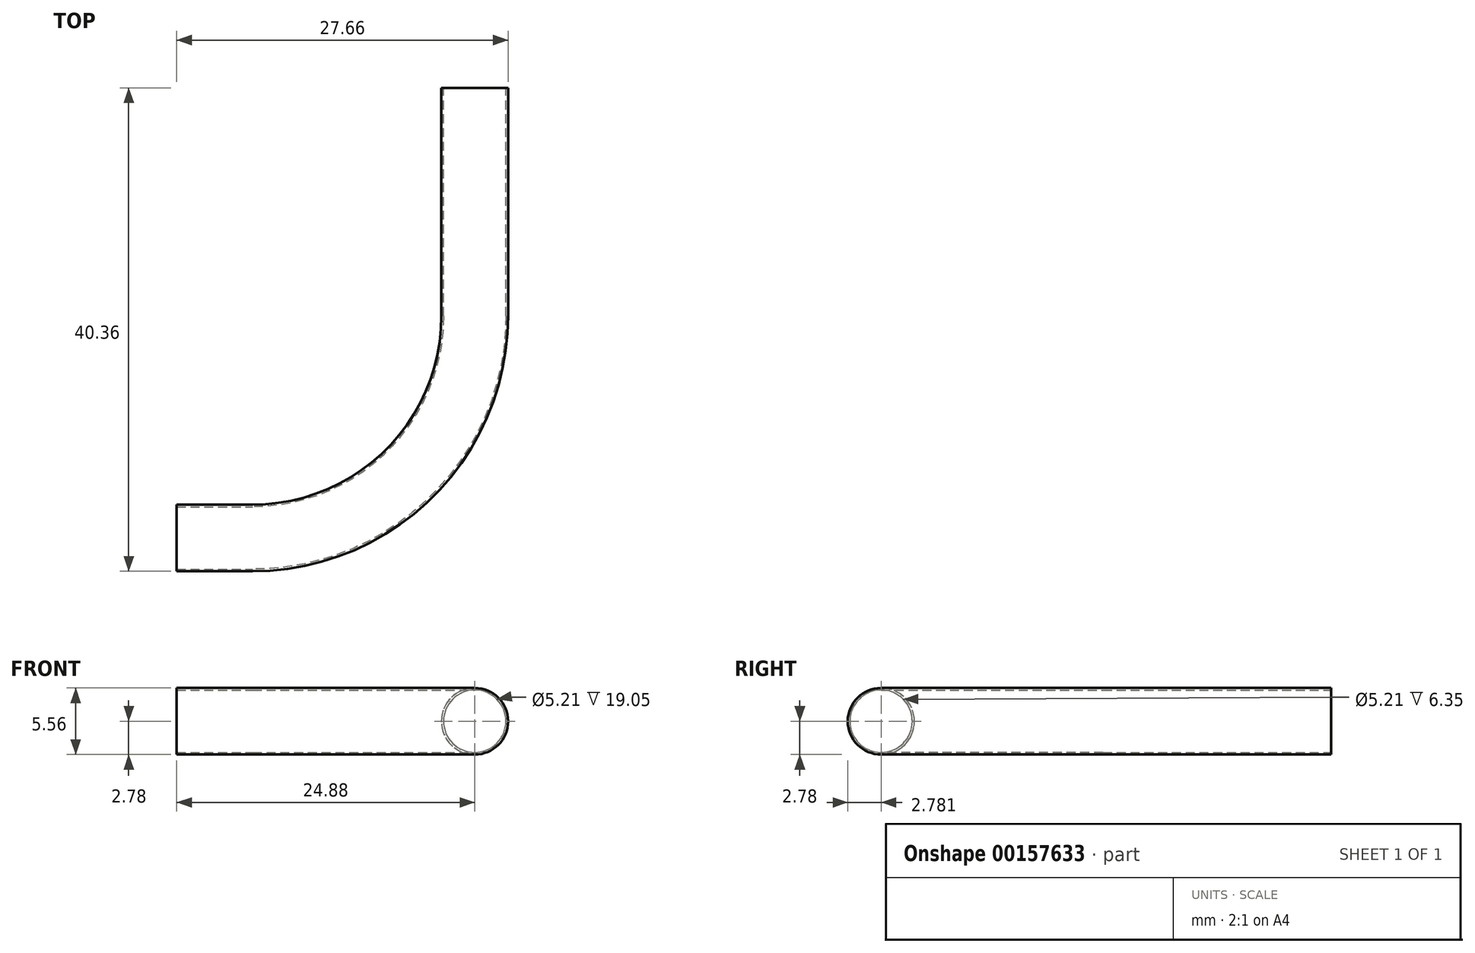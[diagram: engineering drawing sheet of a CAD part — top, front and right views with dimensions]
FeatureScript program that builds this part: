
annotation { "Feature Type Name" : "Feature", "Feature Type Description" : "" }
export const myFeature = defineFeature(function(context is Context, id is Id, definition is map)
    precondition{}
    {
        {
            var Q0;
            Q0=qCreatedBy(makeId("Front.planeOp"),FACE);
            var sketch = newSketch(context, id + "F0", { "sketchPlane" : qUnion([Q0])});
            skCircle(sketch, "E0", {"center": v(0, 0) * mm, "radius": 2.78 * mm});
            skSolve(sketch);
        }
        {
            var Q0;
            Q0=qCreatedBy(makeId("Top.planeOp"),FACE);
            var sketch = newSketch(context, id + "F1", { "sketchPlane" : qUnion([Q0])});
            skLineSegment(sketch, "E1", {"start": v(0, 0) * mm, "end": v(0, -19.05) * mm});
            skLineSegment(sketch, "E2", {"start": v(-18.53, -37.58) * mm, "end": v(-24.88, -37.58) * mm});
            skArc(sketch, "E3", {"start": v(-18.53, -37.58) * mm, "mid": v(-5.43, -32.15) * mm, "end": v(0, -19.05) * mm});
            skSolve(sketch);
        }
        {
            var Q0;
            Q0=makeQuery(id+"F0.imprint","IMPRINT",FACE,{"disambiguationData":[TD([[makeQuery(id+"F0.imprint","IMPRINT",EDGE,{"derivedFrom":sQuery(id+"F0.wireOp",EDGE,"E0")}),1.0]])]});
            var Q1;
            Q1=sQuery(id+"F0.wireOp",EDGE,"E0");
            var Q2;
            Q2=sQuery(id+"F1.wireOp",EDGE,"E1");
            var Q3;
            Q3=sQuery(id+"F1.wireOp",EDGE,"E3");
            var Q4;
            Q4=sQuery(id+"F1.wireOp",EDGE,"E2");
            sweep(context, id + "F2", {"profiles" : qUnion([Q0]), "surfaceProfiles" : qUnion([Q1]), "path" : qUnion([Q2, Q3, Q4])});
        }
        {
            var Q0;
            Q0=makeQuery(id+"F2.opSweep","CAP_FACE",FACE,{"disambiguationData":[OSD([sQuery(id+"F0.wireOp",EDGE,"E0"),sQuery(id+"F1.wireOp",VERTEX,"E2.end")])],"isStart":false});
            var sketch = newSketch(context, id + "F3", { "sketchPlane" : qUnion([Q0])});
            skCircle(sketch, "E4", {"center": v(37.58, 0) * mm, "radius": 2.6 * mm});
            skSolve(sketch);
        }
        {
            var Q0;
            Q0=makeQuery(id+"F3.imprint","IMPRINT",FACE,{"disambiguationData":[TD([[makeQuery(id+"F3.imprint","IMPRINT",EDGE,{"derivedFrom":sQuery(id+"F3.wireOp",EDGE,"E4")}),1.0]])]});
            var Q1;
            Q1 = qConstructionFilter(qBodyType(qCreatedBy(id + "F1" ,EDGE), BodyType.WIRE), ConstructionObject.NO);
            sweep(context, id + "F4", {"operationType" : NewBodyOperationType.REMOVE, "profiles" : qUnion([Q0]), "path" : qUnion([Q1])});
        }
    });
